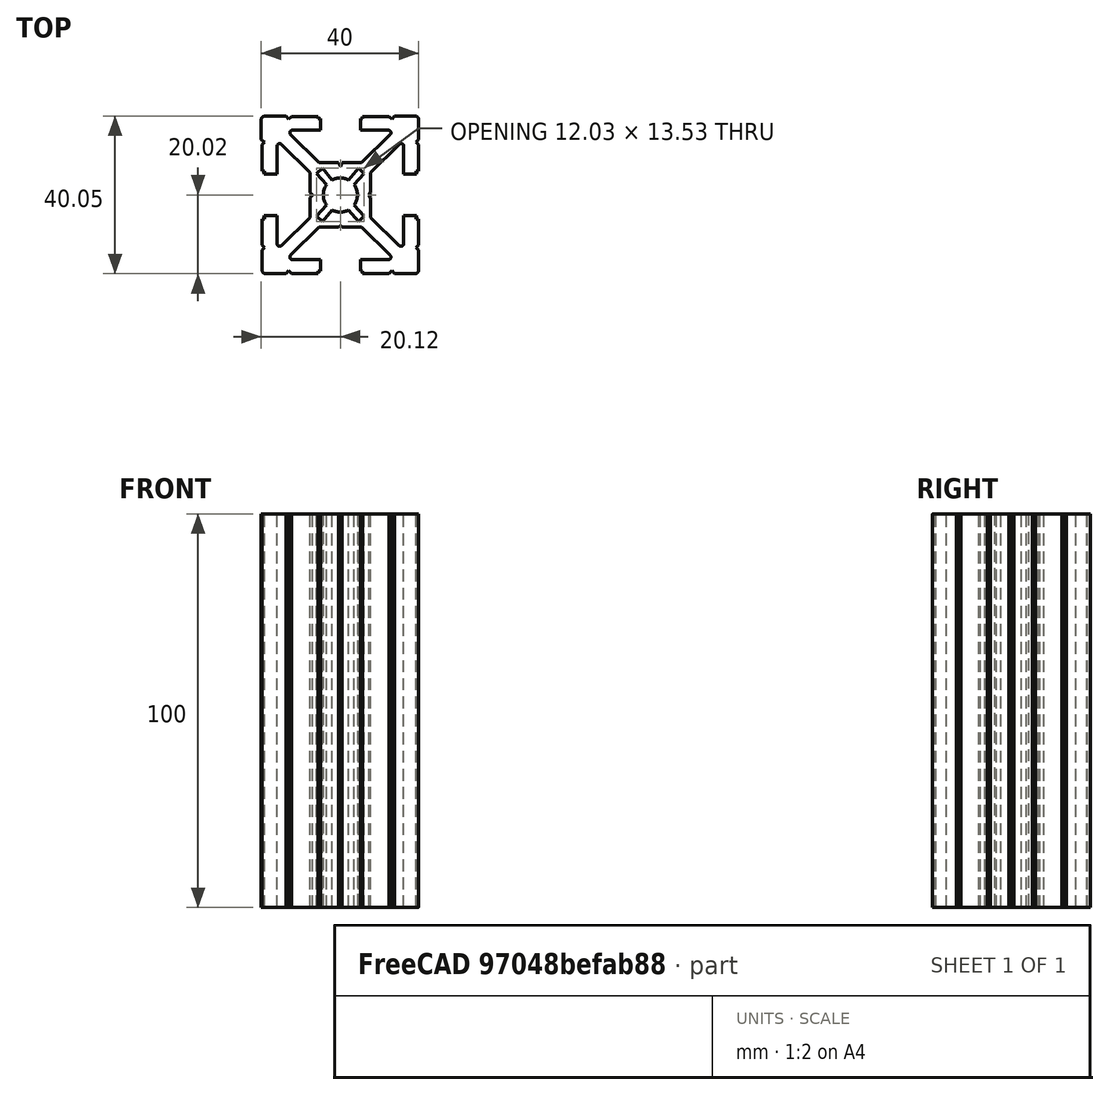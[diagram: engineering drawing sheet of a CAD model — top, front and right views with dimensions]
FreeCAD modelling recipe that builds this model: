
FCSTD DOCUMENT  (FreeCAD 0.17R13509 (Git))
Label: Profile Bosh 40x40mm
License: All rights reserved
LicenseURL: http://en.wikipedia.org/wiki/All_rights_reserved
objects: Sketcher::SketchObject×2, PartDesign::Pad×1, PartDesign::Body×1, App::Part×1
note: 5 computed .brp shape members not serialized (recipe doc carries the construction recipe); baked Part::Feature solids carry a one-line shape summary decoded from their .brp

FEATURE [Sketcher::SketchObject] Sketch
  sketch-geometry (116):
    g0: BSplineCurve PolesCount=2 KnotsCount=2 Degree=1 IsPeriodic=0
    g1: BSplineCurve PolesCount=2 KnotsCount=2 Degree=1 IsPeriodic=0
    g2: BSplineCurve PolesCount=2 KnotsCount=2 Degree=1 IsPeriodic=0
    g3: BSplineCurve PolesCount=3 KnotsCount=2 Degree=2 IsPeriodic=0
    g4: BSplineCurve PolesCount=3 KnotsCount=2 Degree=2 IsPeriodic=0
    g5: BSplineCurve PolesCount=3 KnotsCount=2 Degree=2 IsPeriodic=0
    g6: BSplineCurve PolesCount=3 KnotsCount=2 Degree=2 IsPeriodic=0
    g7: BSplineCurve PolesCount=3 KnotsCount=2 Degree=2 IsPeriodic=0
    g8: BSplineCurve PolesCount=3 KnotsCount=2 Degree=2 IsPeriodic=0
    g9: BSplineCurve PolesCount=3 KnotsCount=2 Degree=2 IsPeriodic=0
    g10: BSplineCurve PolesCount=3 KnotsCount=2 Degree=2 IsPeriodic=0
    g11: BSplineCurve PolesCount=2 KnotsCount=2 Degree=1 IsPeriodic=0
    g12: BSplineCurve PolesCount=2 KnotsCount=2 Degree=1 IsPeriodic=0
    g13: BSplineCurve PolesCount=2 KnotsCount=2 Degree=1 IsPeriodic=0
    g14: BSplineCurve PolesCount=2 KnotsCount=2 Degree=1 IsPeriodic=0
    g15: BSplineCurve PolesCount=2 KnotsCount=2 Degree=1 IsPeriodic=0
    g16: BSplineCurve PolesCount=2 KnotsCount=2 Degree=1 IsPeriodic=0
    g17: BSplineCurve PolesCount=2 KnotsCount=2 Degree=1 IsPeriodic=0
    g18: BSplineCurve PolesCount=2 KnotsCount=2 Degree=1 IsPeriodic=0
    g19: BSplineCurve PolesCount=2 KnotsCount=2 Degree=1 IsPeriodic=0
    g20: BSplineCurve PolesCount=2 KnotsCount=2 Degree=1 IsPeriodic=0
    g21: BSplineCurve PolesCount=2 KnotsCount=2 Degree=1 IsPeriodic=0
    g22: BSplineCurve PolesCount=2 KnotsCount=2 Degree=1 IsPeriodic=0
    g23: BSplineCurve PolesCount=2 KnotsCount=2 Degree=1 IsPeriodic=0
    g24: BSplineCurve PolesCount=2 KnotsCount=2 Degree=1 IsPeriodic=0
    g25: BSplineCurve PolesCount=2 KnotsCount=2 Degree=1 IsPeriodic=0
    g26: BSplineCurve PolesCount=2 KnotsCount=2 Degree=1 IsPeriodic=0
    g27: BSplineCurve PolesCount=2 KnotsCount=2 Degree=1 IsPeriodic=0
    g28: BSplineCurve PolesCount=2 KnotsCount=2 Degree=1 IsPeriodic=0
    g29: BSplineCurve PolesCount=2 KnotsCount=2 Degree=1 IsPeriodic=0
    g30: BSplineCurve PolesCount=2 KnotsCount=2 Degree=1 IsPeriodic=0
    g31: BSplineCurve PolesCount=2 KnotsCount=2 Degree=1 IsPeriodic=0
    g32: BSplineCurve PolesCount=2 KnotsCount=2 Degree=1 IsPeriodic=0
    g33: BSplineCurve PolesCount=2 KnotsCount=2 Degree=1 IsPeriodic=0
    g34: BSplineCurve PolesCount=2 KnotsCount=2 Degree=1 IsPeriodic=0
    g35: BSplineCurve PolesCount=2 KnotsCount=2 Degree=1 IsPeriodic=0
    g36: BSplineCurve PolesCount=2 KnotsCount=2 Degree=1 IsPeriodic=0
    g37: BSplineCurve PolesCount=2 KnotsCount=2 Degree=1 IsPeriodic=0
    g38: BSplineCurve PolesCount=2 KnotsCount=2 Degree=1 IsPeriodic=0
    g39: BSplineCurve PolesCount=2 KnotsCount=2 Degree=1 IsPeriodic=0
    g40: BSplineCurve PolesCount=2 KnotsCount=2 Degree=1 IsPeriodic=0
    g41: BSplineCurve PolesCount=2 KnotsCount=2 Degree=1 IsPeriodic=0
    g42: BSplineCurve PolesCount=2 KnotsCount=2 Degree=1 IsPeriodic=0
    g43: BSplineCurve PolesCount=2 KnotsCount=2 Degree=1 IsPeriodic=0
    g44: BSplineCurve PolesCount=3 KnotsCount=2 Degree=2 IsPeriodic=0
    g45: BSplineCurve PolesCount=2 KnotsCount=2 Degree=1 IsPeriodic=0
    g46: BSplineCurve PolesCount=2 KnotsCount=2 Degree=1 IsPeriodic=0
    g47: BSplineCurve PolesCount=2 KnotsCount=2 Degree=1 IsPeriodic=0
    g48: BSplineCurve PolesCount=2 KnotsCount=2 Degree=1 IsPeriodic=0
    g49: BSplineCurve PolesCount=3 KnotsCount=2 Degree=2 IsPeriodic=0
    g50: BSplineCurve PolesCount=2 KnotsCount=2 Degree=1 IsPeriodic=0
    g51: BSplineCurve PolesCount=3 KnotsCount=2 Degree=2 IsPeriodic=0
    g52: BSplineCurve PolesCount=3 KnotsCount=2 Degree=2 IsPeriodic=0
    g53: BSplineCurve PolesCount=3 KnotsCount=2 Degree=2 IsPeriodic=0
    g54: BSplineCurve PolesCount=2 KnotsCount=2 Degree=1 IsPeriodic=0
    g55: BSplineCurve PolesCount=2 KnotsCount=2 Degree=1 IsPeriodic=0
    g56: BSplineCurve PolesCount=2 KnotsCount=2 Degree=1 IsPeriodic=0
    g57: BSplineCurve PolesCount=2 KnotsCount=2 Degree=1 IsPeriodic=0
    g58: BSplineCurve PolesCount=3 KnotsCount=2 Degree=2 IsPeriodic=0
    g59: BSplineCurve PolesCount=3 KnotsCount=2 Degree=2 IsPeriodic=0
    g60: BSplineCurve PolesCount=3 KnotsCount=2 Degree=2 IsPeriodic=0
    g61: BSplineCurve PolesCount=2 KnotsCount=2 Degree=1 IsPeriodic=0
    g62: BSplineCurve PolesCount=2 KnotsCount=2 Degree=1 IsPeriodic=0
    g63: BSplineCurve PolesCount=2 KnotsCount=2 Degree=1 IsPeriodic=0
    g64: BSplineCurve PolesCount=2 KnotsCount=2 Degree=1 IsPeriodic=0
    g65: BSplineCurve PolesCount=2 KnotsCount=2 Degree=1 IsPeriodic=0
    g66: BSplineCurve PolesCount=2 KnotsCount=2 Degree=1 IsPeriodic=0
    g67: BSplineCurve PolesCount=2 KnotsCount=2 Degree=1 IsPeriodic=0
    g68: BSplineCurve PolesCount=2 KnotsCount=2 Degree=1 IsPeriodic=0
    g69: BSplineCurve PolesCount=2 KnotsCount=2 Degree=1 IsPeriodic=0
    g70: BSplineCurve PolesCount=2 KnotsCount=2 Degree=1 IsPeriodic=0
    g71: BSplineCurve PolesCount=2 KnotsCount=2 Degree=1 IsPeriodic=0
    g72: BSplineCurve PolesCount=2 KnotsCount=2 Degree=1 IsPeriodic=0
    g73: BSplineCurve PolesCount=2 KnotsCount=2 Degree=1 IsPeriodic=0
    g74: BSplineCurve PolesCount=2 KnotsCount=2 Degree=1 IsPeriodic=0
    g75: BSplineCurve PolesCount=2 KnotsCount=2 Degree=1 IsPeriodic=0
    g76: BSplineCurve PolesCount=2 KnotsCount=2 Degree=1 IsPeriodic=0
    g77: BSplineCurve PolesCount=2 KnotsCount=2 Degree=1 IsPeriodic=0
    g78: BSplineCurve PolesCount=2 KnotsCount=2 Degree=1 IsPeriodic=0
    g79: BSplineCurve PolesCount=2 KnotsCount=2 Degree=1 IsPeriodic=0
    g80: BSplineCurve PolesCount=2 KnotsCount=2 Degree=1 IsPeriodic=0
    g81: BSplineCurve PolesCount=2 KnotsCount=2 Degree=1 IsPeriodic=0
    g82: BSplineCurve PolesCount=2 KnotsCount=2 Degree=1 IsPeriodic=0
    g83: BSplineCurve PolesCount=2 KnotsCount=2 Degree=1 IsPeriodic=0
    g84: BSplineCurve PolesCount=2 KnotsCount=2 Degree=1 IsPeriodic=0
    g85: BSplineCurve PolesCount=2 KnotsCount=2 Degree=1 IsPeriodic=0
    g86: BSplineCurve PolesCount=2 KnotsCount=2 Degree=1 IsPeriodic=0
    g87: BSplineCurve PolesCount=2 KnotsCount=2 Degree=1 IsPeriodic=0
    g88: BSplineCurve PolesCount=2 KnotsCount=2 Degree=1 IsPeriodic=0
    g89: BSplineCurve PolesCount=2 KnotsCount=2 Degree=1 IsPeriodic=0
    g90: BSplineCurve PolesCount=2 KnotsCount=2 Degree=1 IsPeriodic=0
    g91: BSplineCurve PolesCount=2 KnotsCount=2 Degree=1 IsPeriodic=0
    g92: BSplineCurve PolesCount=2 KnotsCount=2 Degree=1 IsPeriodic=0
    g93: BSplineCurve PolesCount=2 KnotsCount=2 Degree=1 IsPeriodic=0
    g94: BSplineCurve PolesCount=2 KnotsCount=2 Degree=1 IsPeriodic=0
    g95: BSplineCurve PolesCount=2 KnotsCount=2 Degree=1 IsPeriodic=0
    g96: BSplineCurve PolesCount=2 KnotsCount=2 Degree=1 IsPeriodic=0
    g97: BSplineCurve PolesCount=2 KnotsCount=2 Degree=1 IsPeriodic=0
    g98: BSplineCurve PolesCount=2 KnotsCount=2 Degree=1 IsPeriodic=0
    g99: BSplineCurve PolesCount=2 KnotsCount=2 Degree=1 IsPeriodic=0
    g100: BSplineCurve PolesCount=2 KnotsCount=2 Degree=1 IsPeriodic=0
    g101: BSplineCurve PolesCount=2 KnotsCount=2 Degree=1 IsPeriodic=0
    g102: BSplineCurve PolesCount=2 KnotsCount=2 Degree=1 IsPeriodic=0
    g103: BSplineCurve PolesCount=2 KnotsCount=2 Degree=1 IsPeriodic=0
    g104: BSplineCurve PolesCount=2 KnotsCount=2 Degree=1 IsPeriodic=0
    g105: BSplineCurve PolesCount=2 KnotsCount=2 Degree=1 IsPeriodic=0
    g106: BSplineCurve PolesCount=2 KnotsCount=2 Degree=1 IsPeriodic=0
    g107: BSplineCurve PolesCount=2 KnotsCount=2 Degree=1 IsPeriodic=0
    g108: BSplineCurve PolesCount=2 KnotsCount=2 Degree=1 IsPeriodic=0
    g109: BSplineCurve PolesCount=2 KnotsCount=2 Degree=1 IsPeriodic=0
    g110: BSplineCurve PolesCount=2 KnotsCount=2 Degree=1 IsPeriodic=0
    g111: BSplineCurve PolesCount=2 KnotsCount=2 Degree=1 IsPeriodic=0
    g112: BSplineCurve PolesCount=2 KnotsCount=2 Degree=1 IsPeriodic=0
    g113: BSplineCurve PolesCount=2 KnotsCount=2 Degree=1 IsPeriodic=0
    g114: BSplineCurve PolesCount=2 KnotsCount=2 Degree=1 IsPeriodic=0
    g115: BSplineCurve PolesCount=2 KnotsCount=2 Degree=1 IsPeriodic=0
FEATURE [Sketcher::SketchObject] Sketch001
  MapMode = 5
  Support = -> [XY_Plane001]
  sketch-geometry (118):
    g0: LineSegment StartX=0 StartY=7.2242 StartZ=0 EndX=-0.420682 EndY=8.21975 EndZ=0
    g1: LineSegment StartX=-0.420682 StartY=8.21975 StartZ=0 EndX=-5.43509 EndY=8.21975 EndZ=0
    g2: LineSegment StartX=-5.43509 StartY=8.21975 StartZ=0 EndX=-12.6411 EndY=15.3153 EndZ=0
    g3: LineSegment StartX=-12.1775 StartY=16.4469 StartZ=0 EndX=-5.07583 EndY=16.4469 EndZ=0
    g4: LineSegment StartX=-5.07583 StartY=16.4469 StartZ=0 EndX=-5.07583 EndY=19.3813 EndZ=0
    g5: LineSegment StartX=-5.07583 StartY=19.3813 StartZ=0 EndX=-5.6531 EndY=19.3813 EndZ=0
    g6: LineSegment StartX=-5.6531 StartY=19.3813 StartZ=0 EndX=-5.6531 EndY=19.9586 EndZ=0
    g7: LineSegment StartX=-5.6531 StartY=19.9586 StartZ=0 EndX=-12.4072 EndY=19.9586 EndZ=0
    g8: LineSegment StartX=-12.4072 StartY=19.9586 StartZ=0 EndX=-13.1577 EndY=19.2081 EndZ=0
    g9: LineSegment StartX=-13.1577 StartY=19.2081 StartZ=0 EndX=-13.7927 EndY=19.9837 EndZ=0
    g10: LineSegment StartX=-13.7927 StartY=19.9837 StartZ=0 EndX=-19.2555 EndY=19.9837 EndZ=0
    g11: LineSegment StartX=-20.1184 StartY=19.1209 StartZ=0 EndX=-20.1184 EndY=14.0126 EndZ=0
    g12: LineSegment StartX=-20.1184 StartY=14.0126 StartZ=0 EndX=-19.2768 EndY=13.3776 EndZ=0
    g13: LineSegment StartX=-19.2768 StartY=13.3776 StartZ=0 EndX=-19.8541 EndY=12.8003 EndZ=0
    g14: LineSegment StartX=-19.8541 StartY=12.8003 StartZ=0 EndX=-19.8541 EndY=6.10392 EndZ=0
    g15: LineSegment StartX=-19.8541 StartY=6.10392 StartZ=0 EndX=-19.2191 EndY=6.10392 EndZ=0
    g16: LineSegment StartX=-19.2191 StartY=6.10392 StartZ=0 EndX=-19.3346 EndY=5.29573 EndZ=0
    g17: LineSegment StartX=-19.3346 StartY=5.29573 StartZ=0 EndX=-16.1018 EndY=5.29573 EndZ=0
    g18: LineSegment StartX=-16.1018 StartY=5.29573 StartZ=0 EndX=-16.1018 EndY=12.3583 EndZ=0
    g19: LineSegment StartX=-14.9612 StartY=12.8377 StartZ=0 EndX=-7.67357 EndY=5.69982 EndZ=0
    g20: LineSegment StartX=-7.67357 StartY=5.69982 StartZ=0 EndX=-7.67357 EndY=0.619792 EndZ=0
    g21: LineSegment StartX=-7.67357 StartY=0.619792 StartZ=0 EndX=-7.01151 EndY=0 EndZ=0
    g22: ArcOfCircle CenterX=-19.2555 CenterY=19.1209 CenterZ=0 NormalX=0 NormalY=0 NormalZ=1 AngleXU=0 Radius=0.862818 StartAngle=1.5708 EndAngle=3.14159
    g23: ArcOfCircle CenterX=-15.4308 CenterY=12.3583 CenterZ=0 NormalX=0 NormalY=0 NormalZ=1 AngleXU=0 Radius=0.671038 StartAngle=0.795779 EndAngle=3.14159
    g24: ArcOfCircle CenterX=-12.1775 CenterY=15.7862 CenterZ=0 NormalX=0 NormalY=0 NormalZ=1 AngleXU=0 Radius=0.660753 StartAngle=1.5708 EndAngle=3.93471
    g25: LineSegment [constr] StartX=0 StartY=0 StartZ=0 EndX=0 EndY=7.2242 EndZ=0
    g26: LineSegment [constr] StartX=7.2242 StartY=0 StartZ=0 EndX=0 EndY=0 EndZ=0
    g27: LineSegment StartX=0 StartY=7.2242 StartZ=0 EndX=0.420682 EndY=8.21975 EndZ=0
    g28: LineSegment StartX=0.420682 StartY=8.21975 StartZ=0 EndX=5.43509 EndY=8.21975 EndZ=0
    g29: LineSegment StartX=5.43509 StartY=8.21975 StartZ=0 EndX=12.6411 EndY=15.3153 EndZ=0
    g30: LineSegment StartX=12.1775 StartY=16.4469 StartZ=0 EndX=5.07583 EndY=16.4469 EndZ=0
    g31: LineSegment StartX=5.07583 StartY=16.4469 StartZ=0 EndX=5.07583 EndY=19.3813 EndZ=0
    g32: LineSegment StartX=5.07583 StartY=19.3813 StartZ=0 EndX=5.6531 EndY=19.3813 EndZ=0
    g33: LineSegment StartX=5.6531 StartY=19.3813 StartZ=0 EndX=5.6531 EndY=19.9586 EndZ=0
    g34: LineSegment StartX=5.6531 StartY=19.9586 StartZ=0 EndX=12.4072 EndY=19.9586 EndZ=0
    g35: LineSegment StartX=12.4072 StartY=19.9586 StartZ=0 EndX=13.1577 EndY=19.2081 EndZ=0
    g36: LineSegment StartX=13.1577 StartY=19.2081 StartZ=0 EndX=13.7927 EndY=20.0301 EndZ=0
    g37: LineSegment StartX=13.7927 StartY=20.0301 StartZ=0 EndX=19.0188 EndY=20.0301 EndZ=0
    g38: LineSegment StartX=19.8816 StartY=19.1672 StartZ=0 EndX=19.8816 EndY=14.0126 EndZ=0
    g39: LineSegment StartX=19.8816 StartY=14.0126 StartZ=0 EndX=19.2768 EndY=13.3776 EndZ=0
    g40: LineSegment StartX=19.2768 StartY=13.3776 StartZ=0 EndX=19.8541 EndY=12.8003 EndZ=0
    g41: LineSegment StartX=19.8541 StartY=12.8003 StartZ=0 EndX=19.8541 EndY=6.10392 EndZ=0
    g42: LineSegment StartX=19.8541 StartY=6.10392 StartZ=0 EndX=19.2191 EndY=6.10392 EndZ=0
    g43: ArcOfCircle CenterX=19.0188 CenterY=19.1672 CenterZ=0 NormalX=0 NormalY=0 NormalZ=1 AngleXU=0 Radius=0.862818 StartAngle=0 EndAngle=1.5708
    g44: ArcOfCircle CenterX=15.4308 CenterY=12.3583 CenterZ=0 NormalX=0 NormalY=0 NormalZ=1 AngleXU=0 Radius=0.671038 StartAngle=0 EndAngle=2.34581
    g45: ArcOfCircle CenterX=12.1775 CenterY=15.7862 CenterZ=0 NormalX=0 NormalY=0 NormalZ=1 AngleXU=0 Radius=0.660753 StartAngle=5.49007 EndAngle=7.85398
    g46: LineSegment StartX=19.2191 StartY=6.10392 StartZ=0 EndX=19.3346 EndY=5.29573 EndZ=0
    g47: LineSegment StartX=19.3346 StartY=5.29573 StartZ=0 EndX=16.1018 EndY=5.29573 EndZ=0
    g48: LineSegment StartX=16.1018 StartY=5.29573 StartZ=0 EndX=16.1018 EndY=12.3583 EndZ=0
    g49: LineSegment StartX=14.9612 StartY=12.8377 StartZ=0 EndX=7.67357 EndY=5.69982 EndZ=0
    g50: LineSegment StartX=7.67357 StartY=5.69982 StartZ=0 EndX=7.67357 EndY=0.619792 EndZ=0
    g51: LineSegment StartX=7.67357 StartY=0.619792 StartZ=0 EndX=7.2242 EndY=0 EndZ=0
    g52: LineSegment StartX=0 StartY=-7.80079 StartZ=0 EndX=-0.420682 EndY=-8.21975 EndZ=0
    g53: LineSegment StartX=-0.420682 StartY=-8.21975 StartZ=0 EndX=-5.43509 EndY=-8.21975 EndZ=0
    g54: LineSegment StartX=-5.43509 StartY=-8.21975 StartZ=0 EndX=-12.6411 EndY=-15.3153 EndZ=0
    g55: LineSegment StartX=-12.1775 StartY=-16.4469 StartZ=0 EndX=-5.07583 EndY=-16.4469 EndZ=0
    g56: LineSegment StartX=-5.07583 StartY=-16.4469 StartZ=0 EndX=-5.07583 EndY=-19.3813 EndZ=0
    g57: LineSegment StartX=-5.07583 StartY=-19.3813 StartZ=0 EndX=-5.6531 EndY=-19.3813 EndZ=0
    g58: LineSegment StartX=-5.6531 StartY=-19.3813 StartZ=0 EndX=-5.6531 EndY=-19.9586 EndZ=0
    g59: LineSegment StartX=-5.6531 StartY=-19.9586 StartZ=0 EndX=-12.4072 EndY=-19.9586 EndZ=0
    g60: LineSegment StartX=-12.4072 StartY=-19.9586 StartZ=0 EndX=-13.1577 EndY=-19.2081 EndZ=0
    g61: LineSegment StartX=-13.1577 StartY=-19.2081 StartZ=0 EndX=-13.7927 EndY=-20.0163 EndZ=0
    g62: LineSegment StartX=-13.7927 StartY=-20.0163 StartZ=0 EndX=-19.0051 EndY=-20.0163 EndZ=0
    g63: LineSegment StartX=-19.8541 StartY=-19.1672 StartZ=0 EndX=-19.8541 EndY=-14.0126 EndZ=0
    g64: LineSegment StartX=-19.8541 StartY=-14.0126 StartZ=0 EndX=-19.2768 EndY=-13.3776 EndZ=0
    g65: LineSegment StartX=-19.2768 StartY=-13.3776 StartZ=0 EndX=-19.8541 EndY=-12.8003 EndZ=0
    g66: LineSegment StartX=-19.8541 StartY=-12.8003 StartZ=0 EndX=-19.8541 EndY=-6.10392 EndZ=0
    g67: LineSegment StartX=-19.8541 StartY=-6.10392 StartZ=0 EndX=-19.2191 EndY=-6.10392 EndZ=0
    g68: LineSegment StartX=-19.2191 StartY=-6.10392 StartZ=0 EndX=-19.3346 EndY=-5.29573 EndZ=0
    g69: LineSegment StartX=-19.3346 StartY=-5.29573 StartZ=0 EndX=-16.1018 EndY=-5.29573 EndZ=0
    g70: LineSegment StartX=-16.1018 StartY=-5.29573 StartZ=0 EndX=-16.1018 EndY=-12.3583 EndZ=0
    g71: LineSegment StartX=-14.9612 StartY=-12.8377 StartZ=0 EndX=-7.67357 EndY=-5.69982 EndZ=0
    g72: LineSegment StartX=-7.67357 StartY=-5.69982 StartZ=0 EndX=-7.67357 EndY=-0.619792 EndZ=0
    g73: ArcOfCircle CenterX=-19.0051 CenterY=-19.1672 CenterZ=0 NormalX=0 NormalY=0 NormalZ=1 AngleXU=0 Radius=0.849048 StartAngle=3.14159 EndAngle=4.71239
    g74: ArcOfCircle CenterX=-15.4308 CenterY=-12.3583 CenterZ=0 NormalX=0 NormalY=0 NormalZ=1 AngleXU=0 Radius=0.671038 StartAngle=3.14159 EndAngle=5.48741
    g75: ArcOfCircle CenterX=-12.1775 CenterY=-15.7862 CenterZ=0 NormalX=0 NormalY=0 NormalZ=1 AngleXU=0 Radius=0.660753 StartAngle=2.34848 EndAngle=4.71239
    g76: LineSegment StartX=0 StartY=-7.80079 StartZ=0 EndX=0.420682 EndY=-8.21975 EndZ=0
    g77: LineSegment StartX=0.420682 StartY=-8.21975 StartZ=0 EndX=5.43509 EndY=-8.21975 EndZ=0
    g78: LineSegment StartX=5.43509 StartY=-8.21975 StartZ=0 EndX=12.6411 EndY=-15.3153 EndZ=0
    g79: LineSegment StartX=12.1775 StartY=-16.4469 StartZ=0 EndX=5.07583 EndY=-16.4469 EndZ=0
    g80: LineSegment StartX=5.07583 StartY=-16.4469 StartZ=0 EndX=5.07583 EndY=-19.3813 EndZ=0
    g81: LineSegment StartX=5.07583 StartY=-19.3813 StartZ=0 EndX=5.6531 EndY=-19.3813 EndZ=0
    g82: LineSegment StartX=5.6531 StartY=-19.3813 StartZ=0 EndX=5.6531 EndY=-19.9586 EndZ=0
    g83: LineSegment StartX=5.6531 StartY=-19.9586 StartZ=0 EndX=12.4072 EndY=-19.9586 EndZ=0
    g84: LineSegment StartX=12.4072 StartY=-19.9586 StartZ=0 EndX=13.1577 EndY=-19.2081 EndZ=0
    g85: LineSegment StartX=13.1577 StartY=-19.2081 StartZ=0 EndX=13.7927 EndY=-20.0163 EndZ=0
    g86: LineSegment StartX=13.7927 StartY=-20.0163 StartZ=0 EndX=19.0051 EndY=-20.0163 EndZ=0
    g87: LineSegment StartX=19.8541 StartY=-19.1672 StartZ=0 EndX=19.8541 EndY=-14.0126 EndZ=0
    g88: LineSegment StartX=19.8541 StartY=-14.0126 StartZ=0 EndX=19.2768 EndY=-13.3776 EndZ=0
    g89: LineSegment StartX=19.2768 StartY=-13.3776 StartZ=0 EndX=19.8541 EndY=-12.8003 EndZ=0
    g90: LineSegment StartX=19.8541 StartY=-12.8003 StartZ=0 EndX=19.8541 EndY=-6.10392 EndZ=0
    g91: LineSegment StartX=19.8541 StartY=-6.10392 StartZ=0 EndX=19.2191 EndY=-6.10392 EndZ=0
    g92: ArcOfCircle CenterX=19.0051 CenterY=-19.1672 CenterZ=0 NormalX=0 NormalY=0 NormalZ=1 AngleXU=0 Radius=0.849048 StartAngle=4.71239 EndAngle=6.28319
    g93: ArcOfCircle CenterX=15.4308 CenterY=-12.3583 CenterZ=0 NormalX=0 NormalY=0 NormalZ=1 AngleXU=0 Radius=0.671038 StartAngle=3.93737 EndAngle=6.28319
    g94: ArcOfCircle CenterX=12.1775 CenterY=-15.7862 CenterZ=0 NormalX=0 NormalY=0 NormalZ=1 AngleXU=0 Radius=0.660753 StartAngle=4.71239 EndAngle=7.0763
    g95: LineSegment StartX=19.2191 StartY=-6.10392 StartZ=0 EndX=19.3346 EndY=-5.29573 EndZ=0
    g96: LineSegment StartX=19.3346 StartY=-5.29573 StartZ=0 EndX=16.1018 EndY=-5.29573 EndZ=0
    g97: LineSegment StartX=16.1018 StartY=-5.29573 StartZ=0 EndX=16.1018 EndY=-12.3583 EndZ=0
    g98: LineSegment StartX=14.9612 StartY=-12.8377 StartZ=0 EndX=7.67357 EndY=-5.69982 EndZ=0
    g99: LineSegment StartX=7.67357 StartY=-5.69982 StartZ=0 EndX=7.67357 EndY=-0.619792 EndZ=0
    g100: LineSegment StartX=7.67357 StartY=-0.619792 StartZ=0 EndX=7.2242 EndY=0 EndZ=0
    g101: LineSegment StartX=-7.67357 StartY=-0.619792 StartZ=0 EndX=-7.01151 EndY=0 EndZ=0
    g102: ArcOfCircle CenterX=0 CenterY=0 CenterZ=0 NormalX=0 NormalY=0 NormalZ=1 AngleXU=0 Radius=4.34461 StartAngle=1.06729 EndAngle=2.0743
    g103: LineSegment StartX=-2.09626 StartY=3.80544 StartZ=0 EndX=-4.58638 EndY=6.76319 EndZ=0
    g104: LineSegment StartX=-4.58638 StartY=6.76319 StartZ=0 EndX=-6.01301 EndY=5.3625 EndZ=0
    g105: LineSegment StartX=-6.01301 StartY=5.3625 StartZ=0 EndX=-3.47101 EndY=2.61299 EndZ=0
    g106: LineSegment StartX=2.09626 StartY=3.80544 StartZ=0 EndX=4.58638 EndY=6.76319 EndZ=0
    g107: LineSegment StartX=4.58638 StartY=6.76319 StartZ=0 EndX=6.01301 EndY=5.3625 EndZ=0
    g108: LineSegment StartX=6.01301 StartY=5.3625 StartZ=0 EndX=3.47101 EndY=2.61299 EndZ=0
    g109: LineSegment StartX=2.09626 StartY=-3.80544 StartZ=0 EndX=4.58638 EndY=-6.76319 EndZ=0
    g110: LineSegment StartX=4.58638 StartY=-6.76319 StartZ=0 EndX=6.01301 EndY=-5.3625 EndZ=0
    g111: LineSegment StartX=6.01301 StartY=-5.3625 StartZ=0 EndX=3.47101 EndY=-2.61299 EndZ=0
    g112: LineSegment StartX=-2.09626 StartY=-3.80544 StartZ=0 EndX=-4.58638 EndY=-6.76319 EndZ=0
    g113: LineSegment StartX=-6.01301 StartY=-5.3625 StartZ=0 EndX=-3.47101 EndY=-2.61299 EndZ=0
    g114: LineSegment StartX=-4.58638 StartY=-6.76319 StartZ=0 EndX=-6.01301 EndY=-5.3625 EndZ=0
    g115: ArcOfCircle CenterX=0 CenterY=0 CenterZ=0 NormalX=0 NormalY=0 NormalZ=1 AngleXU=0 Radius=4.34461 StartAngle=2.4963 EndAngle=3.78689
    g116: ArcOfCircle CenterX=0 CenterY=0 CenterZ=0 NormalX=0 NormalY=0 NormalZ=1 AngleXU=0 Radius=4.34461 StartAngle=4.20889 EndAngle=5.21589
    g117: ArcOfCircle CenterX=0 CenterY=0 CenterZ=0 NormalX=0 NormalY=0 NormalZ=1 AngleXU=0 Radius=4.34461 StartAngle=5.63789 EndAngle=6.92848
  constraints (189):
    c: PointOnObject(g0,g-2)
    c: Coincident(g0,g1)
    c: Horizontal(g1)
    c: Coincident(g1,g2)
    c: Horizontal(g3)
    c: Coincident(g3,g4)
    c: Vertical(g4)
    c: Coincident(g4,g5)
    c: Horizontal(g5)
    c: Coincident(g5,g6)
    c: Coincident(g6,g7)
    c: Horizontal(g7)
    c: Coincident(g7,g8)
    c: Coincident(g8,g9)
    c: Coincident(g9,g10)
    c: Horizontal(g10)
    c: Vertical(g11)
    c: Coincident(g11,g12)
    c: Coincident(g12,g13)
    c: Coincident(g13,g14)
    c: Vertical(g14)
    c: Coincident(g14,g15)
    c: Horizontal(g15)
    c: Coincident(g15,g16)
    c: Coincident(g16,g17)
    c: Horizontal(g17)
    c: Coincident(g17,g18)
    c: Vertical(g18)
    c: Coincident(g19,g20)
    c: Vertical(g20)
    c: Coincident(g20,g21)
    c: PointOnObject(g21,g-1)
    c: Tangent(g10,g22) = -1.5708
    c: Tangent(g11,g22) = -1.5708
    c: Tangent(g18,g23) = 1.5708
    c: Tangent(g19,g23) = 1.5708
    c: Tangent(g2,g24) = 1.5708
    c: Tangent(g3,g24) = 1.5708
    c: Coincident(g-1,g25)
    c: PointOnObject(g25,g-2)
    c: Coincident(g26,g25)
    c: Horizontal(g26)
    c: Equal(g26,g25)
    c: Coincident(g27,g28)
    c: Horizontal(g28)
    c: Coincident(g28,g29)
    c: Horizontal(g30)
    c: Coincident(g30,g31)
    c: Vertical(g31)
    c: Coincident(g31,g32)
    c: Horizontal(g32)
    c: Coincident(g32,g33)
    c: Coincident(g33,g34)
    c: Horizontal(g34)
    c: Coincident(g34,g35)
    c: Coincident(g35,g36)
    c: Coincident(g36,g37)
    c: Horizontal(g37)
    c: Vertical(g38)
    c: Coincident(g38,g39)
    c: Coincident(g39,g40)
    c: Coincident(g40,g41)
    c: Vertical(g41)
    c: Coincident(g41,g42)
    c: Horizontal(g42)
    c: Coincident(g42,g46)
    c: Coincident(g46,g47)
    c: Horizontal(g47)
    c: Coincident(g47,g48)
    c: Vertical(g48)
    c: Coincident(g49,g50)
    c: Vertical(g50)
    c: Coincident(g50,g51)
    c: Tangent(g37,g43) = 1.5708
    c: Tangent(g38,g43) = 1.5708
    c: Tangent(g48,g44) = -1.5708
    c: Tangent(g49,g44) = -1.5708
    c: Tangent(g29,g45) = -1.5708
    c: Tangent(g30,g45) = -1.5708
    c: Coincident(g52,g53)
    c: Horizontal(g53)
    c: Coincident(g53,g54)
    c: Horizontal(g55)
    c: Coincident(g55,g56)
    c: Vertical(g56)
    c: Coincident(g56,g57)
    c: Horizontal(g57)
    c: Coincident(g57,g58)
    c: Coincident(g58,g59)
    c: Horizontal(g59)
    c: Coincident(g59,g60)
    c: Coincident(g60,g61)
    c: Coincident(g61,g62)
    c: Horizontal(g62)
    c: Vertical(g63)
    c: Coincident(g63,g64)
    c: Coincident(g64,g65)
    c: Coincident(g65,g66)
    c: Vertical(g66)
    c: Coincident(g66,g67)
    c: Horizontal(g67)
    c: Coincident(g67,g68)
    c: Coincident(g68,g69)
    c: Horizontal(g69)
    c: Coincident(g69,g70)
    c: Vertical(g70)
    c: Coincident(g71,g72)
    c: Vertical(g72)
    c: Coincident(g72,g101)
    c: Tangent(g62,g73) = 1.5708
    c: Tangent(g63,g73) = 1.5708
    c: Tangent(g70,g74) = -1.5708
    c: Tangent(g71,g74) = -1.5708
    c: Tangent(g54,g75) = -1.5708
    c: Tangent(g55,g75) = -1.5708
    c: Coincident(g76,g77)
    c: Horizontal(g77)
    c: Coincident(g77,g78)
    c: Horizontal(g79)
    c: Coincident(g79,g80)
    c: Vertical(g80)
    c: Coincident(g80,g81)
    c: Horizontal(g81)
    c: Coincident(g81,g82)
    c: Coincident(g82,g83)
    c: Horizontal(g83)
    c: Coincident(g83,g84)
    c: Coincident(g84,g85)
    c: Coincident(g85,g86)
    c: Horizontal(g86)
    c: Vertical(g87)
    c: Coincident(g87,g88)
    c: Coincident(g88,g89)
    c: Coincident(g89,g90)
    c: Vertical(g90)
    c: Coincident(g90,g91)
    c: Horizontal(g91)
    c: Coincident(g91,g95)
    c: Coincident(g95,g96)
    c: Horizontal(g96)
    c: Coincident(g96,g97)
    c: Vertical(g97)
    c: Coincident(g98,g99)
    c: Vertical(g99)
    c: Coincident(g99,g100)
    c: Tangent(g86,g92) = -1.5708
    c: Tangent(g87,g92) = -1.5708
    c: Tangent(g97,g93) = 1.5708
    c: Tangent(g98,g93) = 1.5708
    c: Tangent(g78,g94) = 1.5708
    c: Tangent(g79,g94) = 1.5708
    c: Coincident(g21,g101)
    c: Coincident(g100,g51)
    c: Coincident(g0,g25)
    c: Coincident(g27,g0)
    c: Coincident(g26,g51)
    c: Vertical(g58)
    c: Vertical(g82)
    c: Vertical(g33)
    c: Vertical(g6)
    c: DistanceX(g11,g38) = 40
    c: DistanceY(g62,g10) = 40
    c: Coincident(g102,g-1)
    c: Coincident(g103,g104)
    c: Coincident(g104,g105)
    c: Coincident(g106,g107)
    c: Coincident(g107,g108)
    c: Coincident(g112,g114)
    c: Coincident(g114,g113)
    c: Coincident(g109,g110)
    c: Coincident(g110,g111)
    c: PointOnObject(g113,g102)
    c: PointOnObject(g112,g102)
    c: PointOnObject(g109,g102)
    c: PointOnObject(g111,g102)
    c: Coincident(g102,g106)
    c: Coincident(g117,g108)
    c: Equal(g102,g115)
    c: Coincident(g102,g103)
    c: Coincident(g115,g105)
    c: Coincident(g102,g115)
    c: Equal(g115,g116)
    c: PointOnObject(g115,g113)
    c: PointOnObject(g116,g112)
    c: Coincident(g115,g116)
    c: Equal(g116,g117)
    c: PointOnObject(g116,g109)
    c: PointOnObject(g117,g111)
    c: Coincident(g116,g117)
FEATURE [PartDesign::Pad] Pad
  Length = 100
  Length2 = 100
  Profile = -> Sketch001
  Refine = true
  Type = 0
FEATURE [PartDesign::Body] Body
  Group = -> [Sketch001,Pad]
  Origin = -> Origin001
  Tip = -> Pad
FEATURE [App::Part] Part
  Group = -> [Body]
  License = CC BY 3.0
  LicenseURL = http://creativecommons.org/licenses/by/3.0/
  Origin = -> Origin
